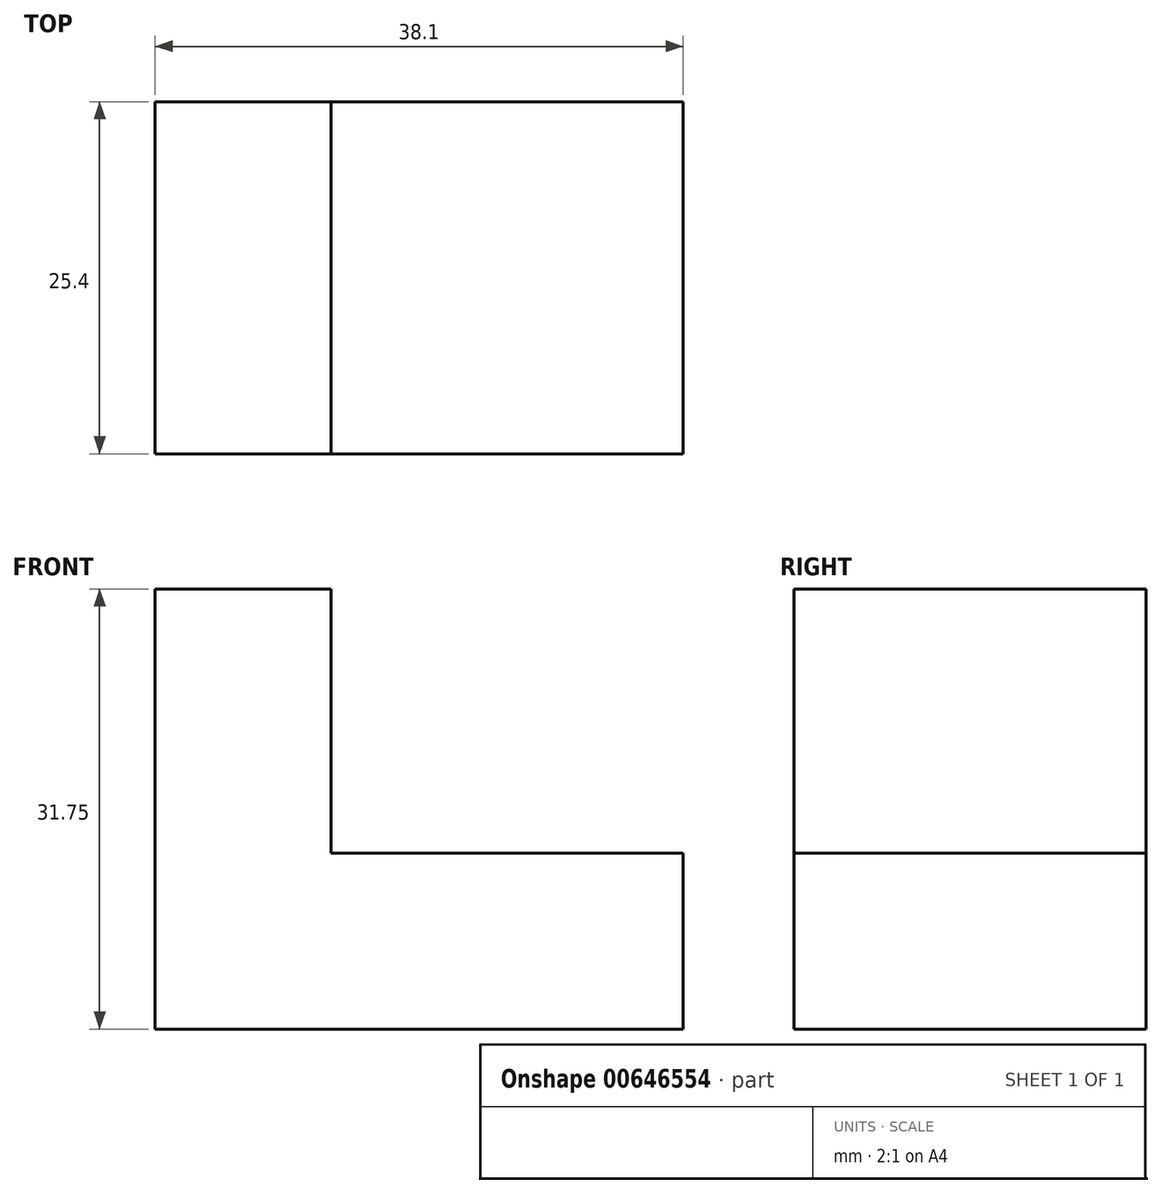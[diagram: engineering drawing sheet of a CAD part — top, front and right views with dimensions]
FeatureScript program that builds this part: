
annotation { "Feature Type Name" : "Feature", "Feature Type Description" : "" }
export const myFeature = defineFeature(function(context is Context, id is Id, definition is map)
    precondition{}
    {
        {
            var Q0;
            Q0=qCreatedBy(makeId("Front.planeOp"),FACE);
            var sketch = newSketch(context, id + "F0", { "sketchPlane" : qUnion([Q0])});
            skLineSegment(sketch, "E0", {"start": v(0, 0) * mm, "end": v(-38.1, 0) * mm});
            skLineSegment(sketch, "E1", {"start": v(-38.1, 0) * mm, "end": v(-38.1, 31.75) * mm});
            skLineSegment(sketch, "E2", {"start": v(-38.1, 31.75) * mm, "end": v(-25.4, 31.75) * mm});
            skLineSegment(sketch, "E3", {"start": v(-25.4, 31.75) * mm, "end": v(-25.4, 12.7) * mm});
            skLineSegment(sketch, "E4", {"start": v(-25.4, 12.7) * mm, "end": v(0, 12.7) * mm});
            skLineSegment(sketch, "E5", {"start": v(0, 12.7) * mm, "end": v(0, 0) * mm});
            skSolve(sketch);
        }
        {
            var Q0;
            Q0=makeQuery(id+"F0.imprint","IMPRINT",FACE,{"disambiguationData":[TD([[makeQuery(id+"F0.imprint","IMPRINT",EDGE,{"derivedFrom":sQuery(id+"F0.wireOp",EDGE,"E0")}),-1.0]])]});
            extrude(context, id + "F1", {"entities" : qUnion([Q0]), "depth" : 25.4 * mm, "offsetDistance" : 25.4 * mm});
        }
    });
